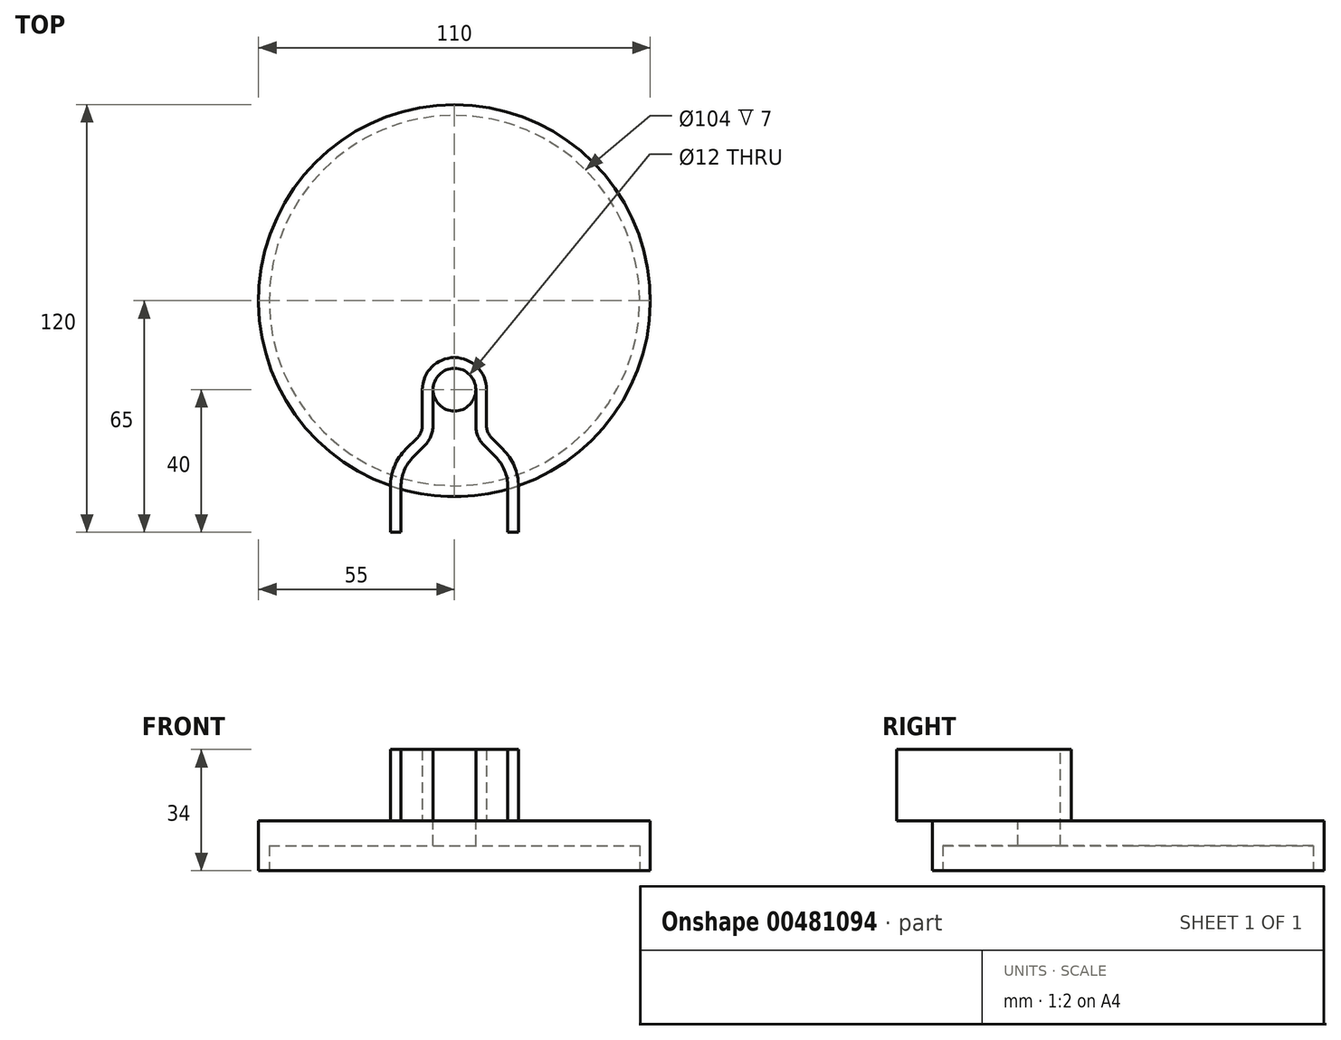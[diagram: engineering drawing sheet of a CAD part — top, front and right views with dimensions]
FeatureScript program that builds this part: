
annotation { "Feature Type Name" : "Feature", "Feature Type Description" : "" }
export const myFeature = defineFeature(function(context is Context, id is Id, definition is map)
    precondition{}
    {
        {
            var Q0;
            Q0=qCreatedBy(makeId("Top.planeOp"),FACE);
            var sketch = newSketch(context, id + "F0", { "sketchPlane" : qUnion([Q0])});
            skCircle(sketch, "E0", {"center": v(0, 0) * mm, "radius": 55 * mm});
            skSolve(sketch);
        }
        {
            var Q0;
            Q0 = qSketchRegion(id + "F0", true);
            extrude(context, id + "F1", {"entities" : qUnion([Q0]), "depth" : 14 * mm});
        }
        {
            var Q0;
            Q0=makeQuery(id+"F1.opExtrude","CAP_FACE",FACE,{"disambiguationData":[OSD([sQuery(id+"F0.wireOp",EDGE,"E0")])],"isStart":true});
            var sketch = newSketch(context, id + "F2", { "sketchPlane" : qUnion([Q0])});
            skCircle(sketch, "E1", {"center": v(0, 0) * mm, "radius": 52 * mm});
            skSolve(sketch);
        }
        {
            var Q0;
            Q0=makeQuery(id+"F2.imprint","IMPRINT",FACE,{"disambiguationData":[TD([[makeQuery(id+"F2.imprint","IMPRINT",EDGE,{"derivedFrom":sQuery(id+"F2.wireOp",EDGE,"E1")}),1.0]])]});
            extrude(context, id + "F3", {"entities" : qUnion([Q0]), "operationType" : NewBodyOperationType.REMOVE, "oppositeDirection" : true, "depth" : 7 * mm});
        }
        {
            var Q0;
            Q0=makeQuery(id+"F1.opExtrude","CAP_FACE",FACE,{"disambiguationData":[OSD([sQuery(id+"F0.wireOp",EDGE,"E0")])],"isStart":false});
            var sketch = newSketch(context, id + "F4", { "sketchPlane" : qUnion([Q0])});
            skCircle(sketch, "E2", {"center": v(0, -25) * mm, "radius": 6 * mm});
            skSolve(sketch);
        }
        {
            var Q0;
            Q0 = qSketchRegion(id + "F4", true);
            extrude(context, id + "F5", {"entities" : qUnion([Q0]), "operationType" : NewBodyOperationType.REMOVE, "endBound" : BoundingType.THROUGH_ALL, "oppositeDirection" : true, "depth" : 25 * mm});
        }
        {
            var Q0;
            Q0=makeQuery(id+"F1.opExtrude","CAP_FACE",FACE,{"disambiguationData":[OSD([sQuery(id+"F0.wireOp",EDGE,"E0")])],"isStart":false});
            var sketch = newSketch(context, id + "F6", { "sketchPlane" : qUnion([Q0])});
            skLineSegment(sketch, "E3", {"start": v(-6, -25) * mm, "end": v(-6, -35) * mm});
            skArc(sketch, "E4", {"start": v(-6, -35) * mm, "mid": v(-6.6, -38.06) * mm, "end": v(-8.34, -40.66) * mm});
            skLineSegment(sketch, "E5", {"start": v(-8.34, -40.66) * mm, "end": v(-11.49, -43.8) * mm});
            skArc(sketch, "E6", {"start": v(-11.49, -43.8) * mm, "mid": v(-14.09, -47.7) * mm, "end": v(-15, -52.28) * mm});
            skLineSegment(sketch, "E7", {"start": v(-15, -52.28) * mm, "end": v(-15, -65) * mm});
            skArc(sketch, "E8", {"start": v(6, -25) * mm, "mid": v(0, -19) * mm, "end": v(-6, -25) * mm});
            skLineSegment(sketch, "E9", {"start": v(0, 0) * mm, "end": v(0, -71.85) * mm, "construction": true});
            skPoint(sketch, "E10.orphan", {"position": v(-6, -25) * mm});
            skArc(sketch, "E11.MirrorCS", {"start": v(11.49, -43.8) * mm, "mid": v(14.09, -47.7) * mm, "end": v(15, -52.28) * mm});
            skLineSegment(sketch, "E12.MirrorCS", {"start": v(8.34, -40.66) * mm, "end": v(11.49, -43.8) * mm});
            skArc(sketch, "E13.MirrorCS", {"start": v(6, -35) * mm, "mid": v(6.6, -38.06) * mm, "end": v(8.34, -40.66) * mm});
            skLineSegment(sketch, "E14.MirrorCS", {"start": v(6, -25) * mm, "end": v(6, -35) * mm});
            skPoint(sketch, "E15.MirrorP", {"position": v(6, -25) * mm});
            skLineSegment(sketch, "E16.MirrorCS", {"start": v(15, -52.28) * mm, "end": v(15, -65) * mm});
            skCircle(sketch, "E17", {"center": v(0, 0) * mm, "radius": 43.5 * mm, "construction": true});
            skLineSegment(sketch, "E18.0", {"start": v(-18, -52.28) * mm, "end": v(-18, -65) * mm});
            skArc(sketch, "E18.1", {"start": v(9, -35) * mm, "mid": v(9.38, -36.91) * mm, "end": v(10.46, -38.54) * mm});
            skLineSegment(sketch, "E18.2", {"start": v(10.46, -38.54) * mm, "end": v(13.6, -41.68) * mm});
            skArc(sketch, "E18.3", {"start": v(13.6, -41.68) * mm, "mid": v(16.86, -46.54) * mm, "end": v(18, -52.28) * mm});
            skLineSegment(sketch, "E18.4", {"start": v(18, -52.28) * mm, "end": v(18, -65) * mm});
            skLineSegment(sketch, "E18.5", {"start": v(9, -25) * mm, "end": v(9, -35) * mm});
            skArc(sketch, "E18.6", {"start": v(9, -25) * mm, "mid": v(0, -16) * mm, "end": v(-9, -25) * mm});
            skLineSegment(sketch, "E18.7", {"start": v(-9, -25) * mm, "end": v(-9, -35) * mm});
            skArc(sketch, "E18.8", {"start": v(-9, -35) * mm, "mid": v(-9.38, -36.91) * mm, "end": v(-10.46, -38.54) * mm});
            skLineSegment(sketch, "E18.9", {"start": v(-10.46, -38.54) * mm, "end": v(-13.6, -41.68) * mm});
            skArc(sketch, "E18.10", {"start": v(-13.6, -41.68) * mm, "mid": v(-16.86, -46.54) * mm, "end": v(-18, -52.28) * mm});
            skLineSegment(sketch, "E19", {"start": v(-18, -65) * mm, "end": v(-15, -65) * mm});
            skLineSegment(sketch, "E20", {"start": v(15, -65) * mm, "end": v(18, -65) * mm});
            skSolve(sketch);
        }
        {
            var Q0;
            {var subQ1=sQuery(id+"F6.wireOp",EDGE,"E18.0");Q0=makeQuery(id+"F6.imprint","IMPRINT",FACE,{"disambiguationData":[TD([[makeQuery(id+"F6.imprint","IMPRINT",EDGE,{"derivedFrom":subQ1}),1.0]])]});}
            var Q1;
            Q1=makeQuery(id+"F6.imprint","IMPRINT",FACE,{"disambiguationData":[TD([[makeQuery(id+"F6.imprint","IMPRINT",EDGE,{"derivedFrom":sQuery(id+"F6.wireOp",EDGE,"E3")}),-1.0]])]});
            var Q2;
            {var subQ0=sQuery(id+"F6.wireOp",EDGE,"E18.4");Q2=makeQuery(id+"F6.imprint","IMPRINT",FACE,{"disambiguationData":[TD([[makeQuery(id+"F6.imprint","IMPRINT",EDGE,{"derivedFrom":subQ0}),-1.0]])]});}
            extrude(context, id + "F7", {"entities" : qUnion([Q0, Q1, Q2]), "operationType" : NewBodyOperationType.ADD, "depth" : 20 * mm});
        }
    });
